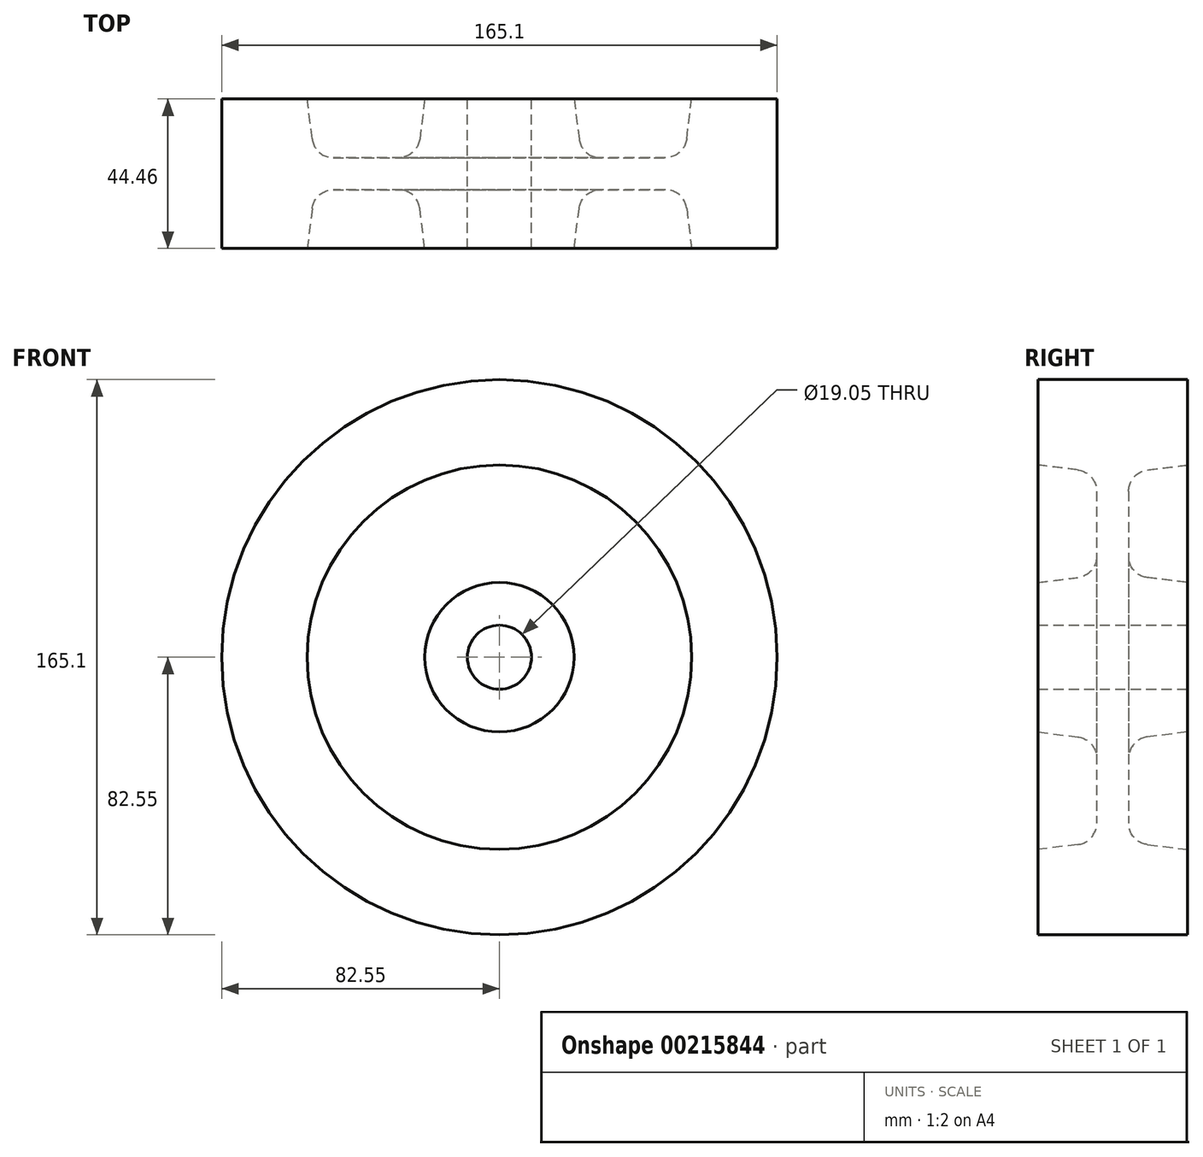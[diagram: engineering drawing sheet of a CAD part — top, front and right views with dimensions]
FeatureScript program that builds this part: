
annotation { "Feature Type Name" : "Feature", "Feature Type Description" : "" }
export const myFeature = defineFeature(function(context is Context, id is Id, definition is map)
    precondition{}
    {
        {
            var Q0;
            Q0=qCreatedBy(makeId("Top.planeOp"),FACE);
            var sketch = newSketch(context, id + "F0", { "sketchPlane" : qUnion([Q0])});
            skLineSegment(sketch, "E0", {"start": v(-9.52, 22.23) * mm, "end": v(-22.23, 22.23) * mm});
            skLineSegment(sketch, "E1", {"start": v(-22.23, 22.23) * mm, "end": v(-23.68, 10.34) * mm});
            skLineSegment(sketch, "E2", {"start": v(-29.99, 4.76) * mm, "end": v(-49.39, 4.76) * mm});
            skLineSegment(sketch, "E3", {"start": v(-55.7, 10.34) * mm, "end": v(-57.15, 22.23) * mm});
            skLineSegment(sketch, "E4", {"start": v(-57.15, 22.23) * mm, "end": v(-82.55, 22.23) * mm});
            skLineSegment(sketch, "E5", {"start": v(-82.55, 22.22) * mm, "end": v(-82.55, 0) * mm});
            skLineSegment(sketch, "E6", {"start": v(-9.53, 22.23) * mm, "end": v(-9.52, 0) * mm});
            skLineSegment(sketch, "E7.MirrorCS", {"start": v(-82.55, -22.22) * mm, "end": v(-82.55, 0) * mm});
            skLineSegment(sketch, "E8.MirrorCS", {"start": v(-57.15, -22.22) * mm, "end": v(-82.55, -22.22) * mm});
            skLineSegment(sketch, "E9.MirrorCS", {"start": v(-55.7, -10.34) * mm, "end": v(-57.15, -22.22) * mm});
            skLineSegment(sketch, "E10.MirrorCS", {"start": v(-29.99, -4.76) * mm, "end": v(-49.39, -4.76) * mm});
            skLineSegment(sketch, "E11.MirrorCS", {"start": v(-22.23, -22.23) * mm, "end": v(-23.68, -10.34) * mm});
            skLineSegment(sketch, "E12.MirrorCS", {"start": v(-9.52, -22.23) * mm, "end": v(-22.23, -22.23) * mm});
            skLineSegment(sketch, "E13.MirrorCS", {"start": v(-9.52, -22.23) * mm, "end": v(-9.52, 0) * mm});
            skPoint(sketch, "E14.visualSharp", {"position": v(-55, 4.76) * mm});
            skArc(sketch, "E14.filletArc", {"start": v(-55.7, 10.34) * mm, "mid": v(-53.6, 6.36) * mm, "end": v(-49.39, 4.76) * mm});
            skPoint(sketch, "E15.visualSharp", {"position": v(-24.37, 4.76) * mm});
            skArc(sketch, "E15.filletArc", {"start": v(-29.99, 4.76) * mm, "mid": v(-25.78, 6.36) * mm, "end": v(-23.68, 10.34) * mm});
            skPoint(sketch, "E16.visualSharp", {"position": v(-55, -4.76) * mm});
            skArc(sketch, "E16.filletArc", {"start": v(-49.39, -4.76) * mm, "mid": v(-53.6, -6.36) * mm, "end": v(-55.7, -10.34) * mm});
            skPoint(sketch, "E17.visualSharp", {"position": v(-24.37, -4.76) * mm});
            skArc(sketch, "E17.filletArc", {"start": v(-23.68, -10.34) * mm, "mid": v(-25.78, -6.36) * mm, "end": v(-29.99, -4.76) * mm});
            skLineSegment(sketch, "E18", {"start": v(0, 48.65) * mm, "end": v(0, -38.39) * mm, "construction": true});
            skSolve(sketch);
        }
        {
            var Q0;
            Q0=qSketchRegion(id+"F0",true);
            var Q1;
            Q1=sQuery(id+"F0.wireOp",EDGE,"E18");
            revolve(context, id + "F1", {"entities" : qUnion([Q0]), "axis" : qUnion([Q1]), "revolveType" : RevolveType.FULL});
        }
    });
